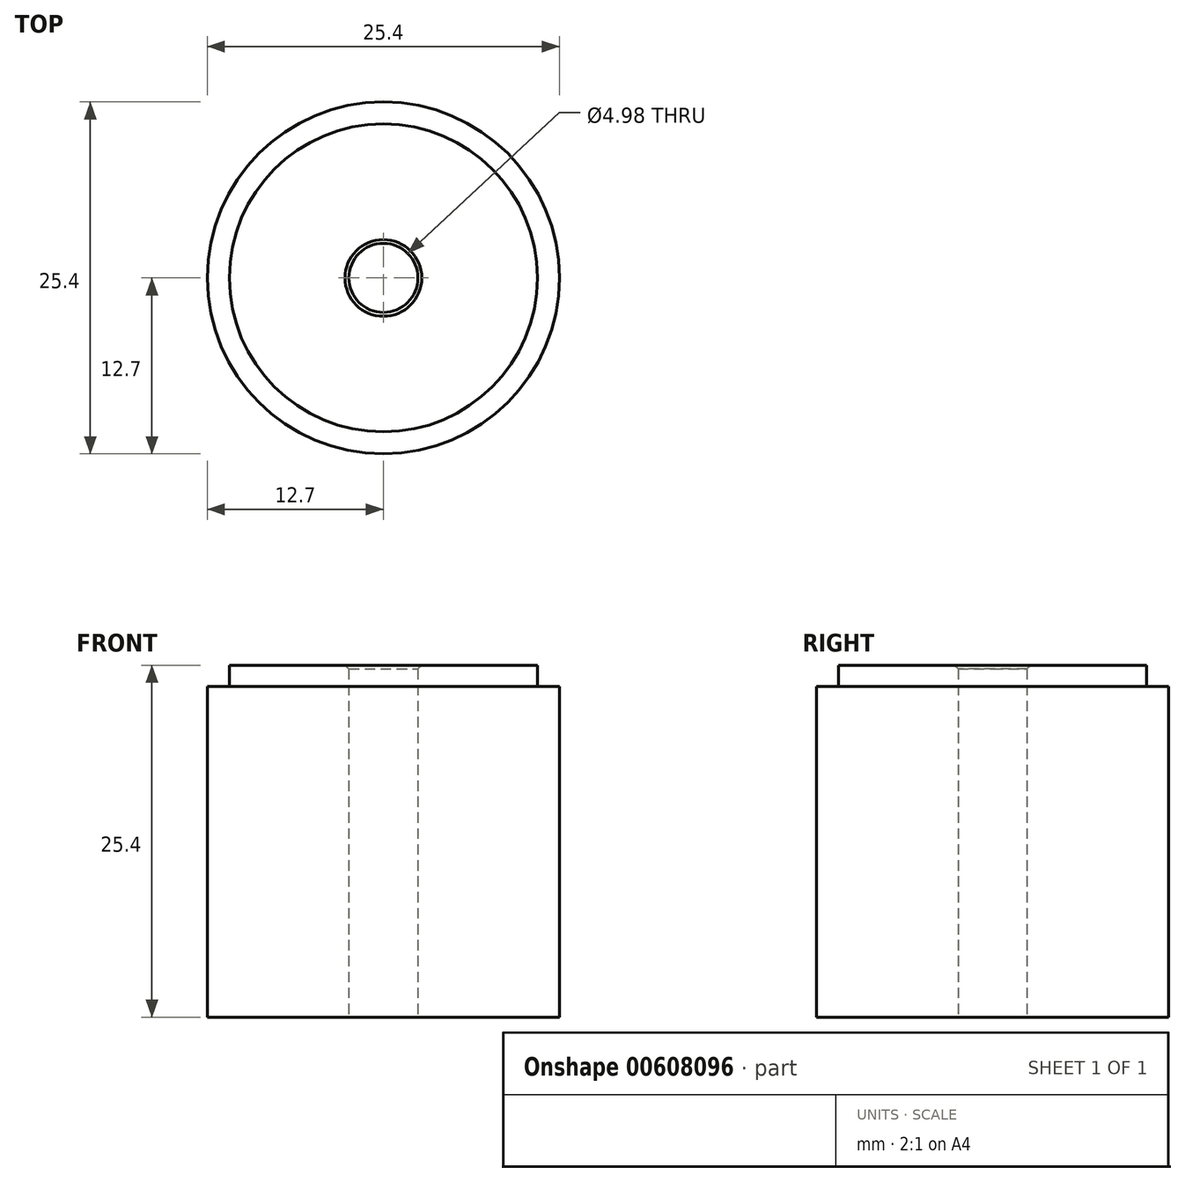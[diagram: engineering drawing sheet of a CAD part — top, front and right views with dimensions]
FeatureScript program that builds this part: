
annotation { "Feature Type Name" : "Feature", "Feature Type Description" : "" }
export const myFeature = defineFeature(function(context is Context, id is Id, definition is map)
    precondition{}
    {
        {
            var Q0;
            Q0=qCreatedBy(makeId("Front.planeOp"),FACE);
            var sketch = newSketch(context, id + "F0", { "sketchPlane" : qUnion([Q0])});
            skLineSegment(sketch, "E0", {"start": v(0, 0) * mm, "end": v(0, 11.58) * mm, "construction": true});
            skLineSegment(sketch, "E1", {"start": v(2.77, 0) * mm, "end": v(11.11, 0) * mm});
            skLineSegment(sketch, "E2", {"start": v(11.11, 0) * mm, "end": v(11.11, -1.52) * mm});
            skLineSegment(sketch, "E3", {"start": v(11.11, -1.52) * mm, "end": v(12.7, -1.52) * mm});
            skLineSegment(sketch, "E4", {"start": v(12.7, -1.52) * mm, "end": v(12.7, -25.4) * mm});
            skLineSegment(sketch, "E5", {"start": v(12.7, -25.4) * mm, "end": v(2.49, -25.4) * mm});
            skLineSegment(sketch, "E6", {"start": v(2.49, -25.4) * mm, "end": v(2.49, -0.28) * mm});
            skLineSegment(sketch, "E7", {"start": v(2.49, -0.28) * mm, "end": v(2.77, 0) * mm});
            skPoint(sketch, "E8.orphan", {"position": v(2.49, 0) * mm});
            skSolve(sketch);
        }
        {
            var Q0;
            Q0 = qSketchRegion(id + "F0", true);
            var Q1;
            Q1=sQuery(id+"F0.wireOp",EDGE,"E0");
            revolve(context, id + "F1", {"entities" : qUnion([Q0]), "axis" : qUnion([Q1]), "revolveType" : RevolveType.FULL});
        }
    });
